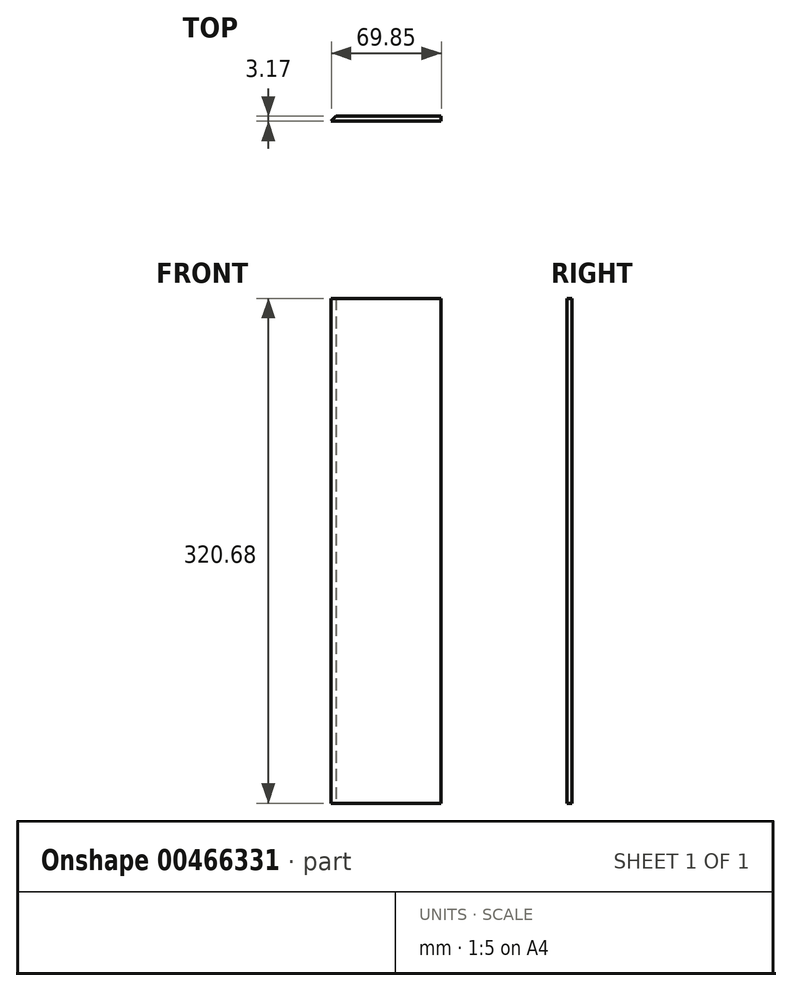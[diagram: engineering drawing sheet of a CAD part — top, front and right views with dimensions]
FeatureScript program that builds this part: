
annotation { "Feature Type Name" : "Feature", "Feature Type Description" : "" }
export const myFeature = defineFeature(function(context is Context, id is Id, definition is map)
    precondition{}
    {
        {
            var Q0;
            Q0=qCreatedBy(makeId("Top.planeOp"),FACE);
            var sketch = newSketch(context, id + "F0", { "sketchPlane" : qUnion([Q0])});
            skLineSegment(sketch, "E0", {"start": v(-44.97, 5.1) * mm, "end": v(-41.8, 8.28) * mm});
            skLineSegment(sketch, "E1", {"start": v(-41.8, 8.28) * mm, "end": v(24.88, 8.28) * mm});
            skLineSegment(sketch, "E2", {"start": v(24.88, 8.28) * mm, "end": v(24.88, 5.1) * mm});
            skLineSegment(sketch, "E3", {"start": v(-44.97, 5.1) * mm, "end": v(24.88, 5.1) * mm});
            skSolve(sketch);
        }
        {
            var Q0;
            Q0 = qSketchRegion(id + "F0", true);
            extrude(context, id + "F1", {"entities" : qUnion([Q0]), "depth" : 320.67 * mm});
        }
    });
